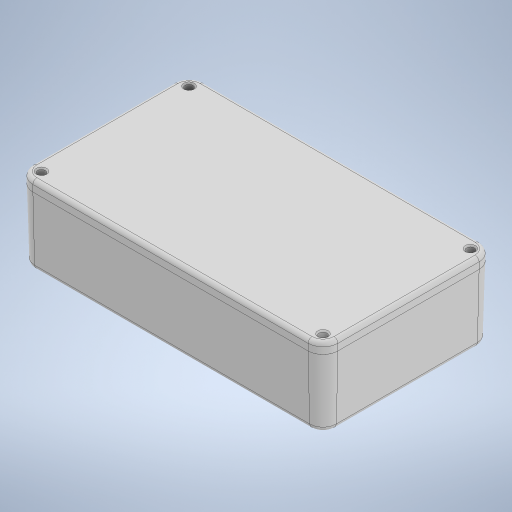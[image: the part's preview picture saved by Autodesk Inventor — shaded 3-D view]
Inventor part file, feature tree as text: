
AUTODESK INVENTOR PART (.ipt)
format: ipt  version: 2023 (Build 270158030, 158C)  size: 605,696 bytes
history: native  units: mm
features: sketch x8, extrude x6, other x4, fillet x3, hole x2, plane x1
ambient origin geometry x8: Origin, YZ Plane, XZ Plane, XY Plane, X Axis, Y Axis, Z Axis, Center Point
bodies: Body1 (feature_tree), Body2 (feature_tree)
feature tree (24):
  other  "Die Cast Box"
  other  "Annotations"
  extrude  "Extrusion1"  Depth=63.6mm
  sketch  "Sketch2"  dims[d2=5.0mm d10=26.3mm d11=0.261799mm]
  plane  "Work Plane1"
  extrude  "Extrusion2"  Depth=5.0mm
  extrude  "Extrusion3"  Depth=1.5mm
  fillet  "Fillet1"  Radius=1.5mm
  sketch  "Sketch4"  dims[d16=4.0mm d17=-1.5mm d18=26.3mm d19=-0.261799mm]
  fillet  "Fillet2"  Radius=1.5mm
  hole  "Hole1"  [1 undecoded]
  extrude  "Extrusion4"  Depth=4.0mm
  fillet  "Fillet3"  Radius=5.3mm
  hole  "Hole2"  [1 undecoded]
  extrude  "Extrusion5"  Depth=3.8mm
  extrude  "Extrusion6"  Depth=1.5mm
  sketch  "Sketch1"  dims[d0=114.5mm d1=63.6mm]
  sketch  "Sketch3"  dims[d12=1.5mm d13=1.5mm d14=1.5mm d15=1.5mm]
  sketch  "Sketch5"  dims[d20=4.0mm d21=4.0mm d22=5.3mm]
  other  "Die Cast Lid"
  sketch  "Sketch6"  dims[d23=3.8mm d24=3.8mm]
  sketch  "Sketch7"  dims[d25=3.8mm d26=3.8mm]
  sketch  "Sketch8"  dims[d27=10.0mm d28=0.0mm d29=1.5mm d30=3.0mm d31=2.0mm d32=2.85mm d33=7.0mm d34=4.0mm d35=2.0mm d36=90.0deg d37=20.0mm d38=20.594885mm d39=5.67mm d40=4.0mm d41=0.0mm d42=1.5mm d43=3.0mm d44=3.0mm d45=7.0mm d46=4.0mm d47=2.0mm d48=90.0deg d49=4.0mm d50=20.594885mm d51=0.5mm d52=0.5mm d53=0.5mm d54=0.5mm d55=1.5mm d56=1.5mm d57=1.5mm d58=1.5mm d59=0.5mm d60=0.5mm d62=10.0mm d63=10.0mm d64=10.0mm d65=10.0mm d66=2.5mm d67=0.0mm d71=9.0mm d72=9.0mm d73=9.0mm d74=9.0mm d75=1.0mm d76=2.5mm d77=0.0mm]
  other  "General Note 1"
note: 2 required parameter values undecoded (feature->parameter linkage not recoverable at this tier; creation-order binding heuristic only, values carry confidence <= 0.55)
